# Revit family: 32_Berkvens_Berlegno RL std + Berklon stomp v0.1
name_source: partatom
category: Doors
units: mm (PartAtom-declared; Revit-internal decimal feet)

## family parameters
Always vertical = Yes
Cut with Voids When Loaded = No
Host = Wall
OmniClass Number = 23.30.10.00
OmniClass Title = Doors
Room Calculation Point = Yes
Shared = No

## types (2) — shared parameters
60_45 Model kozijn = RL enkeldeurs
60_60 Stijllengte = 2630 mm
60_63 Vloerplafondhoogte = 2650 mm  [stored 8.69423 ft]
60_81 Uitvoering kozijn = Kozijn met spiegelstuk
60_84 Type kozijn = Berlegno houten montagekozijn
70_72 Vulling = Vulling : honingraat
70_88 Uitvoering deur = standaard
70_90 Type deur = Berklon, lakdeur
80_30 Krukgathoogte = 1050 mm
80_60 Kantuitvoering = stomp
80_75 Deurhoogte = 2315 mm  [stored 7.59514 ft]
Analytic Construction = <None>
Assembly Code = 2E(32.31.21)
Compartmentation = No
FireExit = No
Function = Interior
IsExternal = No
M1 = Berkvens <maak keuze>
M2 = Berkvens_kristalwit
M3 = Berkvens_reinwit
M4 = Berkvens_reinwit
M5 = Berkvens_kristalwit
M6 = Berkvens_gebroken wit
Manufacturer = Berkvens
Model = Berlegno RL
SelfClosing = No
SmokeStop = No
URL = www.berkvens.nl
Versie = 1.0
Wall Closure = By host
zero-valued in all types: 60_62 Sparingshoogte igv niet verdiepingshoog, Height, Width

## per-type parameters (varying)
| type | 60_51 Sparingsmaat | 80_90 Deurbreedte actieve deur | dbn |
| 930X2315 | 980 mm  [stored 3.21522 ft] | 930 mm  [stored 3.05118 ft] | 926 mm  [stored 3.03806 ft] |
| 730X2315 | 780 mm  [stored 2.55906 ft] | 730 mm  [stored 2.39501 ft] | 726 mm  [stored 2.38189 ft] |

note: [stored X ft] marks values corroborated as IEEE doubles in the binary element streams (Revit-internal decimal feet)

## geometry (parser evidence)
native form markers: Sweep x29
no freeform markers — native parametric forms only
